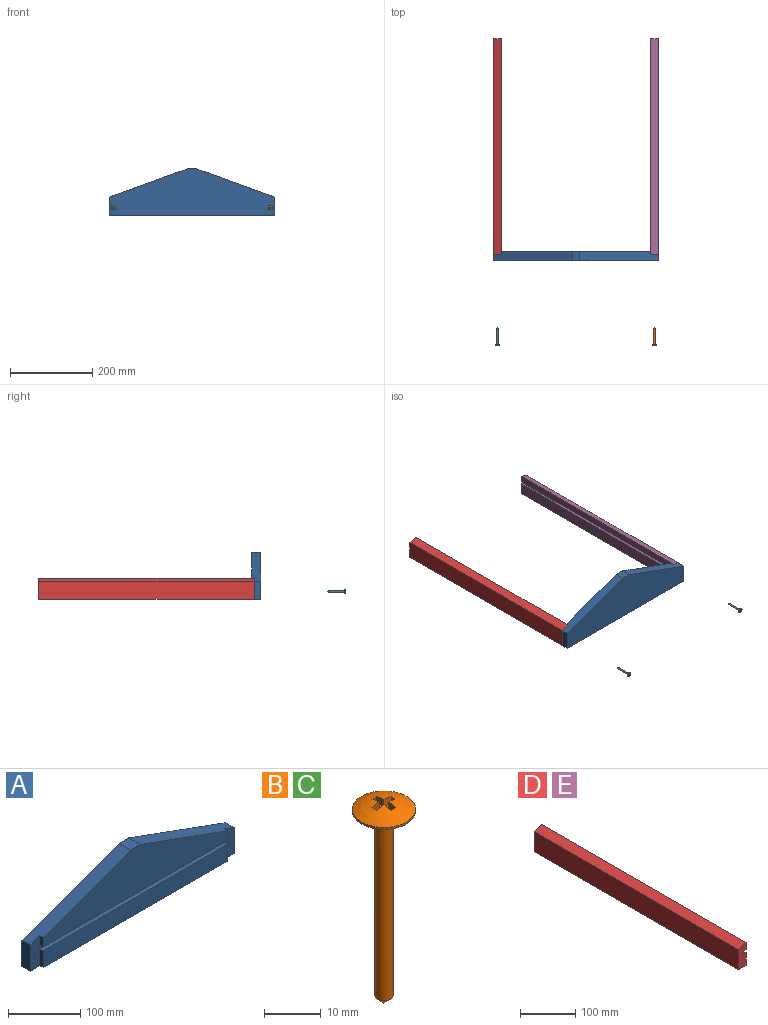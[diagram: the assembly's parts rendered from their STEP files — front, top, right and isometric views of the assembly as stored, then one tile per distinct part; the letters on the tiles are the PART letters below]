
ASSEMBLY  parts=5 mates=4
PART A: 18 faces, bbox 400.1x22.2x113.8 mm
  f0: plane 190.5x69.34mm, normal (0.34,0,0.94), area 4376.9mm2, adj f1,f5,f6,f12,f13,f15
  f1: plane 22.23x19.05mm, normal (0,0,1), area 423.4mm2, adj f0,f2,f6,f15
  f2: plane 190.5x69.34mm, normal (-0.34,0,0.94), area 4376.9mm2, adj f1,f3,f6,f12,f14,f15
  f3: plane 16.46x6.35mm, normal (-1,0,0), area 104.5mm2, adj f2,f4,f6,f12
  f4: plane 361.95x6.35mm, normal (0,0,-1), area 2298.4mm2, adj f3,f5,f6,f12
  f5: plane 16.46x6.35mm, normal (1,0,0), area 104.5mm2, adj f0,f4,f6,f12
  f6: plane 361.95x78.86mm, normal (0,-1,0), area 17844.9mm2, adj f0,f1,f2,f3,f4,f5
  f7: plane 28.58x6.35mm, normal (-1,0,0), area 181.5mm2, adj f8,f10,f11,f12
  f8: plane 400.05x22.23mm, normal (0,0,-1), area 8649.2mm2, adj f7,f9,f11,f12,f13,f14,f15
  f9: plane 28.58x6.35mm, normal (1,0,0), area 181.5mm2, adj f8,f10,f11,f12
  f10: plane 361.95x6.35mm, normal (0,0,1), area 2298.4mm2, adj f7,f9,f11,f12
  f11: plane 361.95x28.58mm, normal (0,-1,0), area 10342.7mm2, adj f7,f8,f9,f10
  f12: plane 400.05x51.38mm, normal (0,-1,0), area 4099.3mm2, adj f0,f2,f3,f4,f5,f7,f8,f9
  f13: plane 44.45x15.88mm, normal (1,0,0), area 705.6mm2, adj f0,f8,f12,f15
  f14: plane 44.45x15.88mm, normal (-1,0,0), area 705.6mm2, adj f2,f8,f12,f15
  f15: plane 400.05x113.79mm, normal (0,1,0), area 32286.9mm2, adj f0,f1,f2,f8,f13,f14,f16,f17
  f16: cylinder r=1.98mm len=15.88mm, axis (0,-1,0), area 197.9mm2, adj f12,f15
  f17: cylinder r=1.98mm len=15.88mm, axis (0,-1,0), area 197.9mm2, adj f12,f15
PART B: 18 faces, bbox 11.1x11.1x43.2 mm
  f0: sphere r=10.52mm, area 94.9mm2, adj f1,f5,f6,f7,f8,f9,f10,f11
  f1: cylinder r=5.56mm len=11.11mm, axis (0,0,-1), area 13.9mm2, adj f0,f2
  f2: plane 11.11x11.11mm, normal (0,0,-1), area 89.1mm2, adj f1,f3
  f3: cylinder r=1.59mm len=39.69mm, axis (0,0,-1), area 395.9mm2, adj f2,f4
  f4: cone r=1.59mm half-angle=45deg, axis (0,0,1), area 11.2mm2, adj f3
  f5: plane 1.31x1.19mm, normal (0,-1,0), area 1.6mm2, adj f0,f6,f16,f17
  f6: plane 1.79x1.55mm, normal (1,0,0), area 2.6mm2, adj f0,f5,f7,f17
  f7: plane 1.79x1.55mm, normal (0,-1,0), area 2.6mm2, adj f0,f6,f8,f17
  f8: plane 1.31x1.19mm, normal (1,0,0), area 1.6mm2, adj f0,f7,f9,f17
  f9: plane 1.79x1.55mm, normal (0,1,0), area 2.6mm2, adj f0,f8,f10,f17
  f10: plane 1.79x1.55mm, normal (1,0,0), area 2.6mm2, adj f0,f9,f11,f17
  f11: plane 1.31x1.19mm, normal (0,1,0), area 1.6mm2, adj f0,f10,f12,f17
  f12: plane 1.79x1.55mm, normal (-1,0,0), area 2.6mm2, adj f0,f11,f13,f17
  f13: plane 1.79x1.55mm, normal (0,1,0), area 2.6mm2, adj f0,f12,f14,f17
  f14: plane 1.31x1.19mm, normal (-1,0,0), area 1.6mm2, adj f0,f13,f15,f17
  f15: plane 1.79x1.55mm, normal (0,-1,0), area 2.6mm2, adj f0,f14,f16,f17
  f16: plane 1.79x1.55mm, normal (-1,0,0), area 2.6mm2, adj f0,f5,f15,f17
  f17: plane 4.76x4.76mm, normal (0,0,1), area 9.9mm2, adj f5,f6,f7,f8,f9,f10,f11,f12
PART C: same geometry as B
PART D: 10 faces, bbox 19.1x523.9x51.4 mm
  f0: plane 523.88x16.46mm, normal (1,0,0), area 8622.3mm2, adj f1,f7,f8,f9
  f1: plane 523.88x19.05mm, normal (-0.34,0,0.94), area 10620.3mm2, adj f0,f2,f8,f9
  f2: plane 523.88x44.45mm, normal (-1,0,0), area 23286.2mm2, adj f1,f3,f8,f9
  f3: plane 523.88x19.05mm, normal (0,0,-1), area 9979.8mm2, adj f2,f4,f8,f9
  f4: plane 523.88x28.58mm, normal (1,0,0), area 14969.7mm2, adj f3,f5,f8,f9
  f5: plane 523.88x6.35mm, normal (0,0,1), area 3326.6mm2, adj f4,f6,f8,f9
  f6: plane 523.88x6.35mm, normal (1,0,0), area 3326.6mm2, adj f5,f7,f8,f9
  f7: plane 523.88x6.35mm, normal (0,0,-1), area 3326.6mm2, adj f0,f6,f8,f9
  f8: plane 51.38x19.05mm, normal (0,-1,0), area 872.5mm2, adj f0,f1,f2,f3,f4,f5,f6,f7
  f9: plane 51.38x19.05mm, normal (0,1,0), area 872.5mm2, adj f0,f1,f2,f3,f4,f5,f6,f7
PART E: same geometry as D
PLACE A rot(axis=(0,0,-1),180deg) t=(5.34,-13.37,0)mm fixed
PLACE B rot(axis=(0,0.71,-0.71),180deg) t=(252.2,-232.84,-12.7)mm
PLACE C rot(axis=(0,0.71,-0.71),180deg) t=(-128.8,-232.84,-12.7)mm
PLACE D t=(30.74,510.5,0)mm
PLACE E rot(axis=(0,0,-1),180deg) t=(-20.06,-13.37,0)mm
MATE fastened B.f1 <-> A.f16  axis (0,1,0) through (195.84,-232.45,-12.7)mm
MATE fastened A.f8 <-> E.f3  axis (0,0,-1) through (205.36,-13.37,-31.75)mm
MATE fastened D.f3 <-> A.f8  axis (0,0,-1) through (-194.69,-13.37,-31.75)mm
MATE fastened A.f17 <-> C.f1  axis (0,-1,0) through (-185.16,-29.25,-12.7)mm
